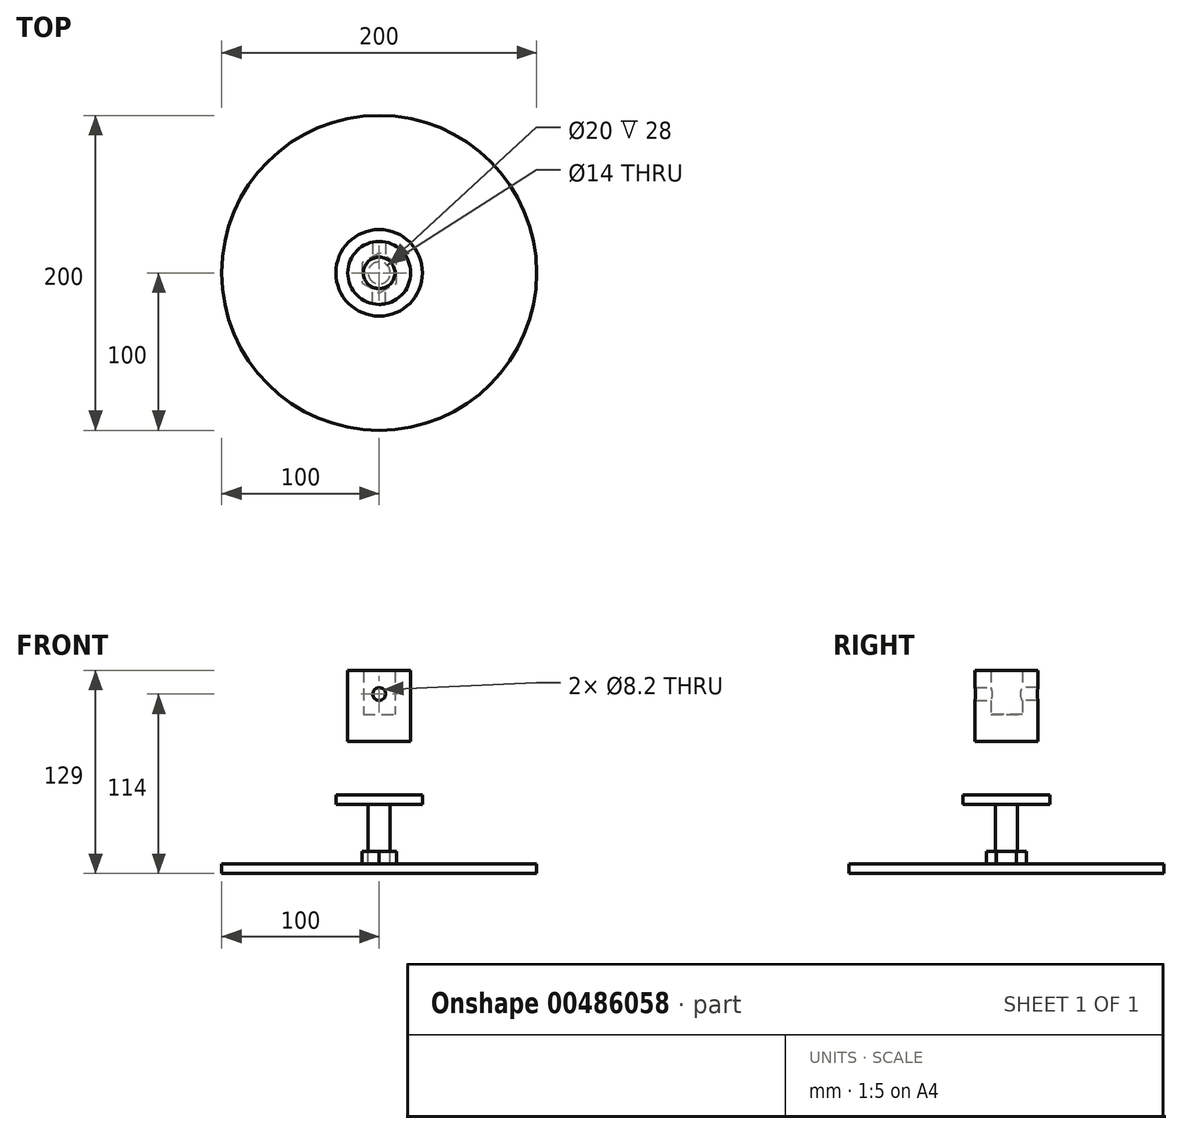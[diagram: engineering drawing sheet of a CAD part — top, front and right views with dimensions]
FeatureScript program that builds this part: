
annotation { "Feature Type Name" : "Feature", "Feature Type Description" : "" }
export const myFeature = defineFeature(function(context is Context, id is Id, definition is map)
    precondition{}
    {
        {
            var Q0;
            Q0=qCreatedBy(makeId("Top.planeOp"),FACE);
            var sketch = newSketch(context, id + "F0", { "sketchPlane" : qUnion([Q0])});
            skCircle(sketch, "E0", {"center": v(0, 0) * mm, "radius": 27.5 * mm});
            skPoint(sketch, "E1", {"position": v(17.5, 0) * mm});
            skPoint(sketch, "E2", {"position": v(0, -17.5) * mm});
            skPoint(sketch, "E3", {"position": v(-17.5, 0) * mm});
            skPoint(sketch, "E4", {"position": v(0, 17.5) * mm});
            skSolve(sketch);
        }
        {
            var Q0;
            Q0 = qSketchRegion(id + "F0", true);
            extrude(context, id + "F1", {"entities" : qUnion([Q0]), "depth" : 6 * mm, "offsetDistance" : 25 * mm});
        }
        {
            var Q0;
            Q0=makeQuery(id+"F0.imprint","IMPRINT",FACE,{"disambiguationData":[TD([[makeQuery(id+"F0.imprint","IMPRINT",EDGE,{"derivedFrom":sQuery(id+"F0.wireOp",EDGE,"E0")}),1.0]])]});
            var sketch = newSketch(context, id + "F2", { "sketchPlane" : qUnion([Q0])});
            skCircle(sketch, "E5", {"center": v(0, 0) * mm, "radius": 7 * mm});
            skSolve(sketch);
        }
        {
            var Q0;
            Q0=makeQuery(id+"F2.imprint","IMPRINT",FACE,{"disambiguationData":[TD([[makeQuery(id+"F2.imprint","IMPRINT",EDGE,{"derivedFrom":sQuery(id+"F2.wireOp",EDGE,"E5")}),1.0]])]});
            extrude(context, id + "F3", {"entities" : qUnion([Q0]), "operationType" : NewBodyOperationType.ADD, "oppositeDirection" : true, "depth" : 30 * mm, "offsetDistance" : 25 * mm});
        }
        {
            var Q0;
            Q0=makeQuery(id+"F3.opExtrude","CAP_FACE",FACE,{"disambiguationData":[OSD([sQuery(id+"F2.wireOp",EDGE,"E5")])],"isStart":false});
            var sketch = newSketch(context, id + "F4", { "sketchPlane" : qUnion([Q0])});
            skCircle(sketch, "E6.cCircle", {"center": v(0, 0) * mm, "radius": 11 * mm, "construction": true});
            skLineSegment(sketch, "E6.0", {"start": v(11, 6.35) * mm, "end": v(11, -6.35) * mm});
            skLineSegment(sketch, "E6.1", {"start": v(11, -6.35) * mm, "end": v(0, -12.7) * mm});
            skLineSegment(sketch, "E6.2", {"start": v(0, -12.7) * mm, "end": v(-11, -6.35) * mm});
            skLineSegment(sketch, "E6.3", {"start": v(-11, -6.35) * mm, "end": v(-11, 6.35) * mm});
            skLineSegment(sketch, "E6.4", {"start": v(-11, 6.35) * mm, "end": v(0, 12.7) * mm});
            skLineSegment(sketch, "E6.5", {"start": v(0, 12.7) * mm, "end": v(11, 6.35) * mm});
            skPoint(sketch, "E6.0.midPoint", {"position": v(11, 0) * mm});
            skSolve(sketch);
        }
        {
            var Q0;
            Q0=makeQuery(id+"F4.imprint","IMPRINT",FACE,{"disambiguationData":[TD([[makeQuery(id+"F4.imprint","IMPRINT",EDGE,{"derivedFrom":sQuery(id+"F4.wireOp",EDGE,"E6.0")}),-1.0]])]});
            extrude(context, id + "F5", {"entities" : qUnion([Q0]), "depth" : 8 * mm, "offsetDistance" : 25 * mm});
        }
        {
            var Q0;
            Q0=makeQuery(id+"F5.opExtrude","CAP_FACE",FACE,{"disambiguationData":[OSD([sQuery(id+"F2.wireOp",EDGE,"E5"),sQuery(id+"F4.wireOp",EDGE,"E6.0"),sQuery(id+"F4.wireOp",EDGE,"E6.1"),sQuery(id+"F4.wireOp",EDGE,"E6.2"),sQuery(id+"F4.wireOp",EDGE,"E6.3"),sQuery(id+"F4.wireOp",EDGE,"E6.4"),sQuery(id+"F4.wireOp",EDGE,"E6.5")])],"isStart":false});
            var sketch = newSketch(context, id + "F6", { "sketchPlane" : qUnion([Q0])});
            skCircle(sketch, "E7", {"center": v(0, 0) * mm, "radius": 100 * mm});
            skCircle(sketch, "E8", {"center": v(0, 0) * mm, "radius": 102 * mm});
            skSolve(sketch);
        }
        {
            var Q0;
            Q0=makeQuery(id+"F6.imprint","IMPRINT",FACE,{"disambiguationData":[TD([[makeQuery(id+"F6.imprint","IMPRINT",EDGE,{"derivedFrom":sQuery(id+"F6.wireOp",EDGE,"E7")}),1.0]])]});
            var Q1;
            Q1=makeQuery(id+"F6.imprint","IMPRINT",FACE,{"disambiguationData":[TD([[makeQuery(id+"F6.imprint","IMPRINT",EDGE,{"derivedFrom":makeQuery(id+"F5.opExtrude","CAP_EDGE",EDGE,{"disambiguationData":[OSD([sQuery(id+"F2.wireOp",EDGE,"E5")])],"isStart":false})}),-1.0]])]});
            var Q2;
            Q2=makeQuery(id+"F6.imprint","IMPRINT",FACE,{"disambiguationData":[TD([[makeQuery(id+"F6.imprint","IMPRINT",EDGE,{"derivedFrom":makeQuery(id+"F5.opExtrude","CAP_EDGE",EDGE,{"disambiguationData":[OSD([sQuery(id+"F4.wireOp",EDGE,"E6.0")])],"isStart":false})}),-1.0]])]});
            extrude(context, id + "F7", {"entities" : qUnion([Q0, Q1, Q2]), "depth" : 6 * mm, "offsetDistance" : 25 * mm});
        }
        {
            var Q0;
            Q0=qCreatedBy(makeId("Front.planeOp"),FACE);
            var sketch = newSketch(context, id + "F8", { "sketchPlane" : qUnion([Q0])});
            skLineSegment(sketch, "E9.bottom", {"start": v(0, 40) * mm, "end": v(-20, 40) * mm});
            skLineSegment(sketch, "E9.top", {"start": v(-10, 85) * mm, "end": v(-20, 85) * mm});
            skLineSegment(sketch, "E9.left", {"start": v(0, 40) * mm, "end": v(0, 57) * mm});
            skLineSegment(sketch, "E9.right", {"start": v(-20, 40) * mm, "end": v(-20, 85) * mm});
            skLineSegment(sketch, "E10", {"start": v(-10, 85) * mm, "end": v(-10, 57) * mm});
            skLineSegment(sketch, "E11", {"start": v(-10, 57) * mm, "end": v(0, 57) * mm});
            skPoint(sketch, "E12", {"position": v(0, 70) * mm});
            skSolve(sketch);
        }
        {
            var Q0;
            Q0=makeQuery(id+"F8.imprint","IMPRINT",FACE,{"disambiguationData":[TD([[makeQuery(id+"F8.imprint","IMPRINT",EDGE,{"derivedFrom":sQuery(id+"F8.wireOp",EDGE,"E9.bottom")}),-1.0]])]});
            var Q1;
            Q1=sQuery(id+"F8.wireOp",EDGE,"E9.left");
            revolve(context, id + "F9", {"surfaceOperationType" : NewSurfaceOperationType.NEW, "entities" : qUnion([Q0]), "axis" : qUnion([Q1]), "revolveType" : RevolveType.FULL});
        }
        {
            var Q0;
            Q0=sQuery(id+"F8.wireOp",VERTEX,"E12");
            var Q1;
            Q1=makeQuery(id+"F9.opRevolve","SWEPT_BODY",BODY,{"disambiguationData":[OSD([sQuery(id+"F8.wireOp",EDGE,"E9.bottom"),sQuery(id+"F8.wireOp",EDGE,"E9.top"),sQuery(id+"F8.wireOp",EDGE,"E9.right"),sQuery(id+"F8.wireOp",EDGE,"E10"),sQuery(id+"F8.wireOp",EDGE,"E11"),sQuery(id+"F8.wireOp",EDGE,"E9.left")])]});
            hole(context, id + "F10", {"style" : HoleStyle.SIMPLE, "endStyle" : HoleEndStyle.BLIND, "holeDiameter" : 8.2 * mm, "majorDiameter" : 5 * mm, "holeDepth" : 30 * mm, "isTappedThrough" : true, "tappedDepth" : 12 * mm, "tapClearance" : 3, "locations" : qUnion([Q0]), "scope" : qUnion([Q1])});
        }
        {
            var Q0;
            Q0=sQuery(id+"F8.wireOp",VERTEX,"E12");
            var Q1;
            Q1=makeQuery(id+"F9.opRevolve","SWEPT_BODY",BODY,{"disambiguationData":[OSD([sQuery(id+"F8.wireOp",EDGE,"E9.bottom"),sQuery(id+"F8.wireOp",EDGE,"E9.top"),sQuery(id+"F8.wireOp",EDGE,"E9.right"),sQuery(id+"F8.wireOp",EDGE,"E10"),sQuery(id+"F8.wireOp",EDGE,"E11"),sQuery(id+"F8.wireOp",EDGE,"E9.left")])]});
            hole(context, id + "F11", {"style" : HoleStyle.SIMPLE, "endStyle" : HoleEndStyle.BLIND, "oppositeDirection" : true, "holeDiameter" : 8.2 * mm, "majorDiameter" : 5 * mm, "holeDepth" : 30 * mm, "isTappedThrough" : true, "tappedDepth" : 12 * mm, "tapClearance" : 3, "locations" : qUnion([Q0]), "scope" : qUnion([Q1])});
        }
    });
